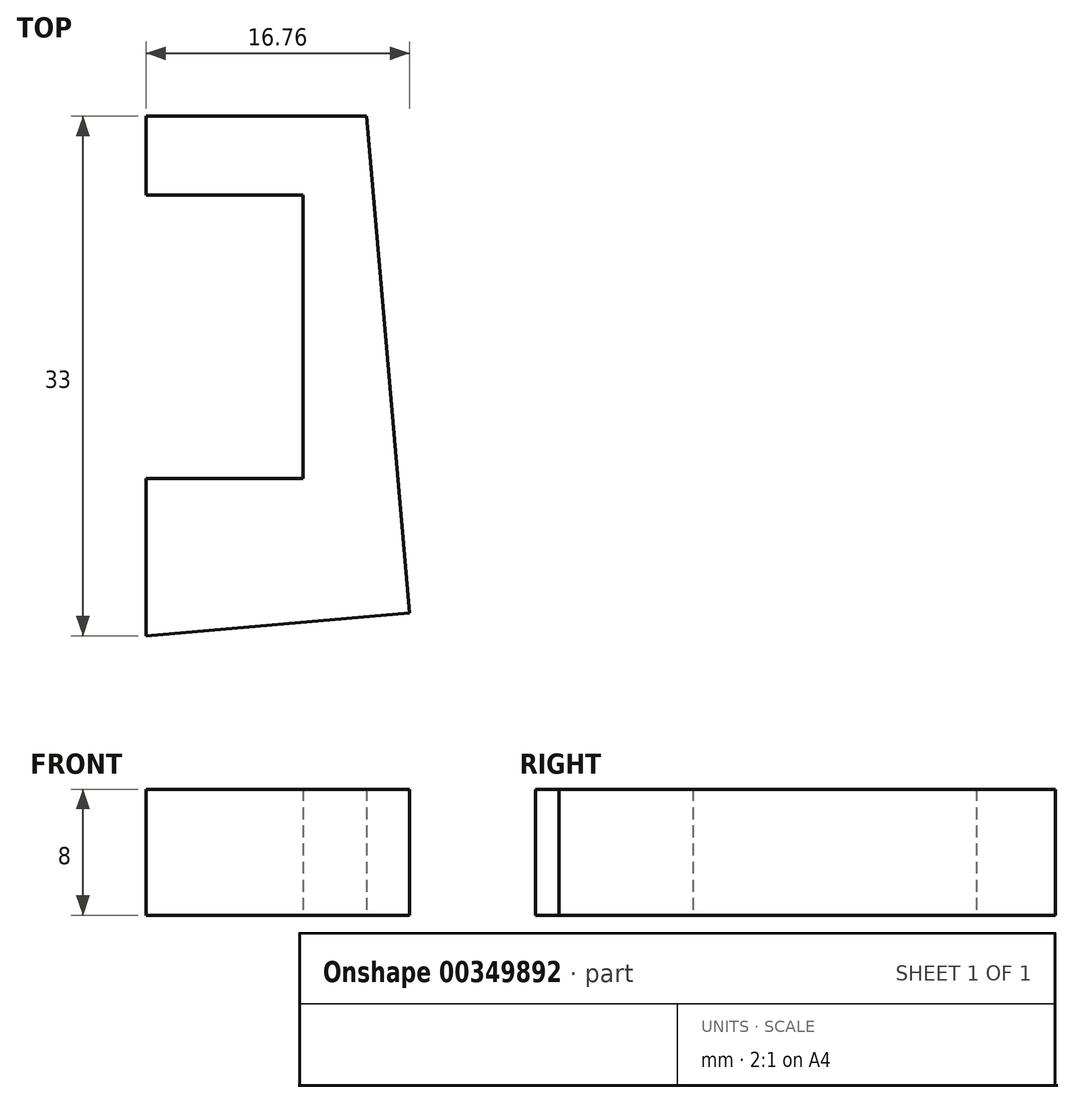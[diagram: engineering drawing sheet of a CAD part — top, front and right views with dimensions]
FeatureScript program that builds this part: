
annotation { "Feature Type Name" : "Feature", "Feature Type Description" : "" }
export const myFeature = defineFeature(function(context is Context, id is Id, definition is map)
    precondition{}
    {
        {
            var Q0;
            Q0=qCreatedBy(makeId("Top.planeOp"),FACE);
            var sketch = newSketch(context, id + "F0", { "sketchPlane" : qUnion([Q0])});
            skLineSegment(sketch, "E0", {"start": v(0, 0) * mm, "end": v(10, 0) * mm});
            skLineSegment(sketch, "E1", {"start": v(10, 0) * mm, "end": v(10, 18) * mm});
            skLineSegment(sketch, "E2", {"start": v(10, 18) * mm, "end": v(0, 18) * mm});
            skLineSegment(sketch, "E3", {"start": v(0, 18) * mm, "end": v(0, 23) * mm});
            skLineSegment(sketch, "E4", {"start": v(0, 0) * mm, "end": v(0, -10) * mm});
            skLineSegment(sketch, "E5", {"start": v(16.76, -8.53) * mm, "end": v(14, 23) * mm});
            skLineSegment(sketch, "E6", {"start": v(14, 23) * mm, "end": v(0, 23) * mm});
            skLineSegment(sketch, "E7", {"start": v(0, -10) * mm, "end": v(16.76, -8.53) * mm});
            skSolve(sketch);
        }
        {
            var Q0;
            Q0=makeQuery(id+"F0.imprint","IMPRINT",FACE,{"disambiguationData":[TD([[makeQuery(id+"F0.imprint","IMPRINT",EDGE,{"derivedFrom":sQuery(id+"F0.wireOp",EDGE,"E0")}),-1.0]])]});
            extrude(context, id + "F1", {"entities" : qUnion([Q0]), "depth" : 8 * mm});
        }
    });
